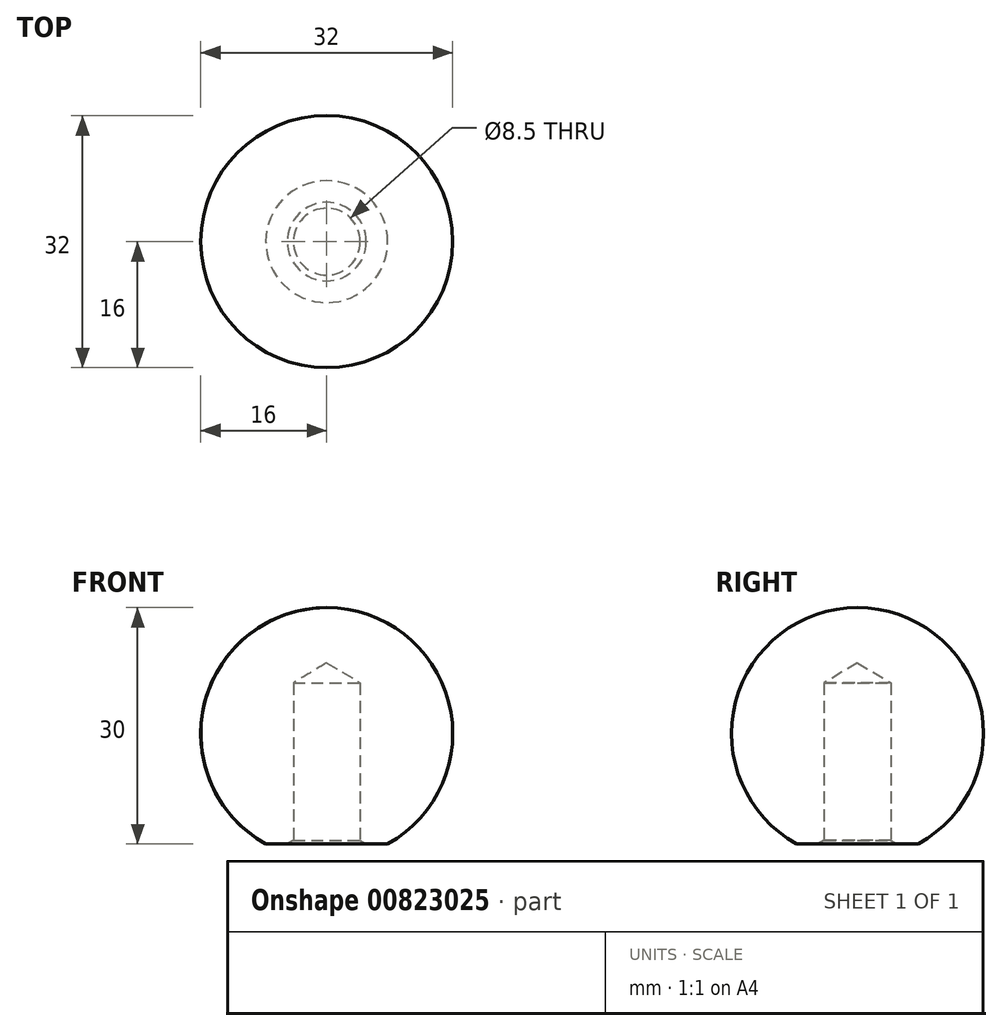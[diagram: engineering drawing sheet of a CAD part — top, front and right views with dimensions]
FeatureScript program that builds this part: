
annotation { "Feature Type Name" : "Feature", "Feature Type Description" : "" }
export const myFeature = defineFeature(function(context is Context, id is Id, definition is map)
    precondition{}
    {
        {
            var Q0;
            Q0=qCreatedBy(makeId("Front.planeOp"),FACE);
            var sketch = newSketch(context, id + "F0", { "sketchPlane" : qUnion([Q0])});
            skLineSegment(sketch, "E0", {"start": v(0, 0) * mm, "end": v(0, 23) * mm, "construction": true});
            skLineSegment(sketch, "E1", {"start": v(0, 23) * mm, "end": v(-4.25, 20.45) * mm});
            skLineSegment(sketch, "E2", {"start": v(-4.25, 20.45) * mm, "end": v(-4.25, 0.43) * mm});
            skLineSegment(sketch, "E3", {"start": v(-4.25, 0.43) * mm, "end": v(-5, 0) * mm});
            skLineSegment(sketch, "E4", {"start": v(-5, 0) * mm, "end": v(-7.75, 0) * mm});
            skLineSegment(sketch, "E5", {"start": v(-24.43, 30) * mm, "end": v(16, 30) * mm, "construction": true});
            skLineSegment(sketch, "E6", {"start": v(16, 30) * mm, "end": v(16, -1.86) * mm, "construction": true});
            skArc(sketch, "E7", {"start": v(0, 30) * mm, "mid": v(-15.5, 18) * mm, "end": v(-7.75, 0) * mm});
            skLineSegment(sketch, "E8", {"start": v(0, 23) * mm, "end": v(0, 30) * mm});
            skSolve(sketch);
        }
        {
            var Q0;
            Q0=makeQuery(id+"F0.imprint","IMPRINT",FACE,{"disambiguationData":[TD([[makeQuery(id+"F0.imprint","IMPRINT",EDGE,{"derivedFrom":sQuery(id+"F0.wireOp",EDGE,"E1")}),-1.0]])]});
            var Q1;
            Q1=sQuery(id+"F0.wireOp",EDGE,"E0");
            revolve(context, id + "F1", {"surfaceOperationType" : NewSurfaceOperationType.NEW, "entities" : qUnion([Q0]), "axis" : qUnion([Q1]), "revolveType" : RevolveType.FULL});
        }
    });
